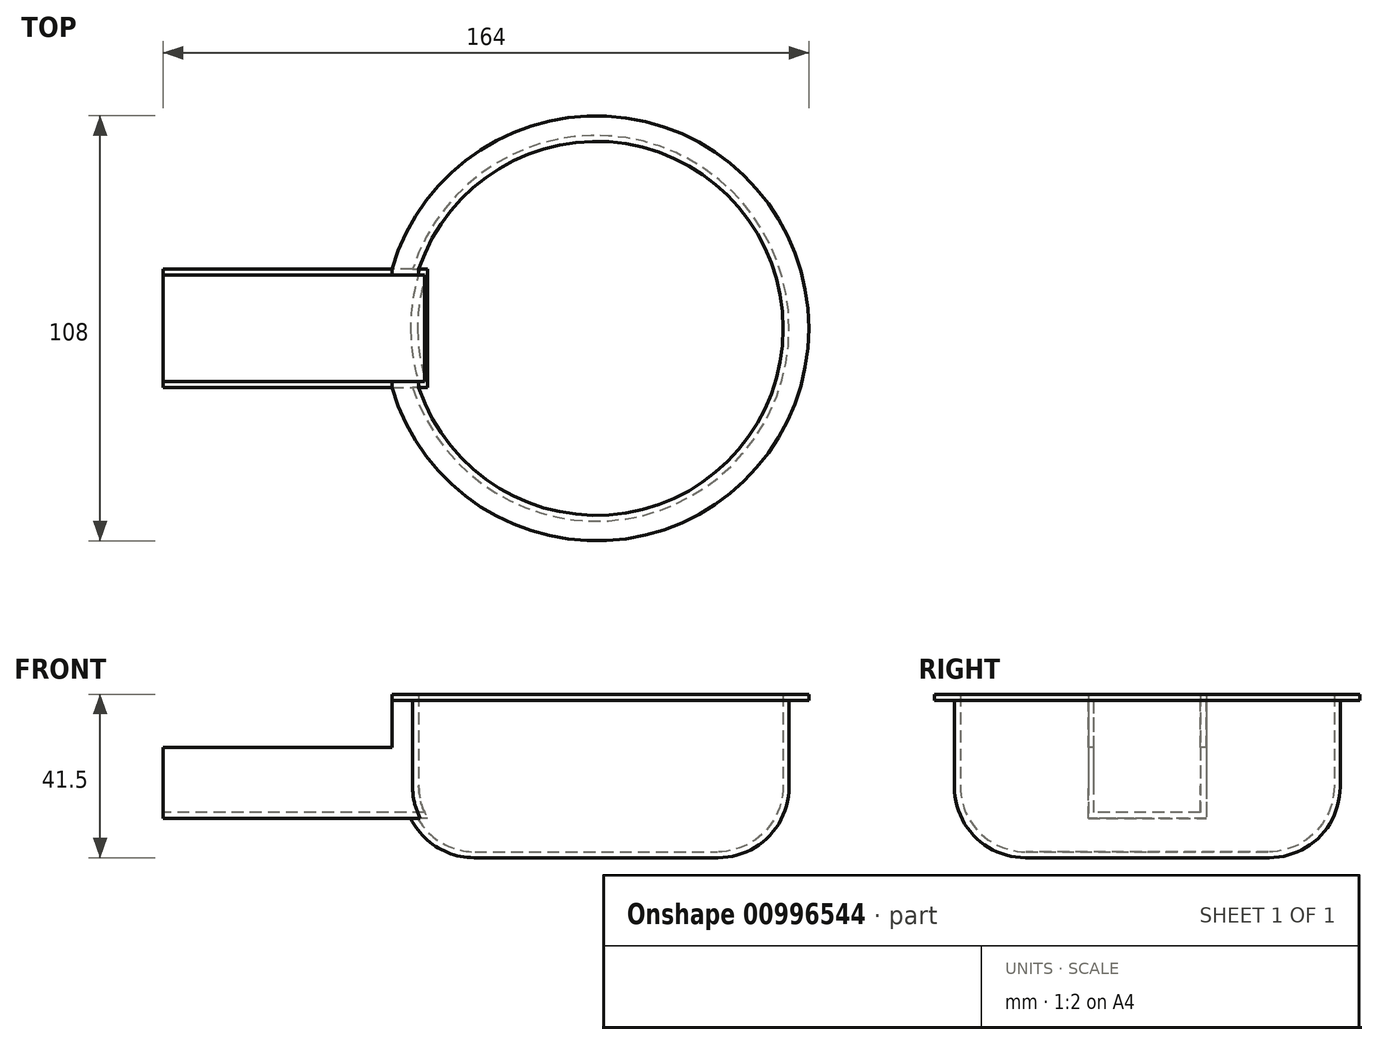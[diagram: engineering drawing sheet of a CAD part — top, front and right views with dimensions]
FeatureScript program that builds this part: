
annotation { "Feature Type Name" : "Feature", "Feature Type Description" : "" }
export const myFeature = defineFeature(function(context is Context, id is Id, definition is map)
    precondition{}
    {
        {
            var Q0;
            Q0=qCreatedBy(makeId("Top.planeOp"),FACE);
            var sketch = newSketch(context, id + "F0", { "sketchPlane" : qUnion([Q0])});
            skLineSegment(sketch, "E0", {"start": v(0, 0) * mm, "end": v(0, 15) * mm});
            skLineSegment(sketch, "E1", {"start": v(0, 15) * mm, "end": v(-110, 15) * mm});
            skLineSegment(sketch, "E2", {"start": v(-110, 15) * mm, "end": v(-110, -15) * mm});
            skLineSegment(sketch, "E3", {"start": v(-110, -15) * mm, "end": v(0, -15) * mm});
            skLineSegment(sketch, "E4", {"start": v(0, -15) * mm, "end": v(0, 0) * mm});
            skSolve(sketch);
        }
        {
            var Q0;
            Q0=qCreatedBy(makeId("Front.planeOp"),FACE);
            var sketch = newSketch(context, id + "F1", { "sketchPlane" : qUnion([Q0])});
            skLineSegment(sketch, "E5", {"start": v(0, 0) * mm, "end": v(30.8, 0) * mm});
            skLineSegment(sketch, "E6", {"start": v(47.5, 16.7) * mm, "end": v(47.5, 40) * mm});
            skLineSegment(sketch, "E7", {"start": v(47.5, 40) * mm, "end": v(54, 40) * mm});
            skLineSegment(sketch, "E8", {"start": v(54, 40) * mm, "end": v(54, 38.5) * mm});
            skLineSegment(sketch, "E9", {"start": v(54, 38.5) * mm, "end": v(49, 38.5) * mm});
            skLineSegment(sketch, "E10", {"start": v(49, 38.5) * mm, "end": v(49, 16.5) * mm});
            skLineSegment(sketch, "E11", {"start": v(31, -1.5) * mm, "end": v(0, -1.5) * mm});
            skLineSegment(sketch, "E12", {"start": v(0, -1.5) * mm, "end": v(0, 0) * mm});
            skPoint(sketch, "E13.visualSharp", {"position": v(47.5, 0) * mm});
            skArc(sketch, "E13.filletArc", {"start": v(30.8, 0) * mm, "mid": v(42.6, 4.9) * mm, "end": v(47.5, 16.7) * mm});
            skPoint(sketch, "E14.visualSharp", {"position": v(49, -1.5) * mm});
            skArc(sketch, "E14.filletArc", {"start": v(31, -1.5) * mm, "mid": v(43.73, 3.77) * mm, "end": v(49, 16.5) * mm});
            skLineSegment(sketch, "E15", {"start": v(0, 0) * mm, "end": v(0, 40) * mm});
            skLineSegment(sketch, "E16", {"start": v(0, 40) * mm, "end": v(47.5, 40) * mm});
            skSolve(sketch);
        }
        {
            var Q0;
            Q0=makeQuery(id+"F0.imprint","IMPRINT",FACE,{"disambiguationData":[TD([[makeQuery(id+"F0.imprint","IMPRINT",EDGE,{"derivedFrom":sQuery(id+"F0.wireOp",EDGE,"E0")}),1.0]])]});
            extrude(context, id + "F2", {"entities" : qUnion([Q0]), "depth" : 40 * mm, "offsetDistance" : 25 * mm});
        }
        {
            var Q0;
            Q0=makeQuery(id+"F0.imprint","IMPRINT",FACE,{"disambiguationData":[TD([[makeQuery(id+"F0.imprint","IMPRINT",EDGE,{"derivedFrom":sQuery(id+"F0.wireOp",EDGE,"E0")}),1.0]])]});
            extrude(context, id + "F3", {"entities" : qUnion([Q0]), "operationType" : NewBodyOperationType.REMOVE, "depth" : 8.5 * mm, "offsetDistance" : 25 * mm});
        }
        {
            var Q0;
            Q0=makeQuery(id+"F2.opExtrude","SWEPT_FACE",FACE,{"disambiguationData":[OSD([sQuery(id+"F0.wireOp",EDGE,"E2")])]});
            var sketch = newSketch(context, id + "F4", { "sketchPlane" : qUnion([Q0])});
            skLineSegment(sketch, "E17", {"start": v(-15, 40) * mm, "end": v(-13.5, 40) * mm});
            skLineSegment(sketch, "E18", {"start": v(-13.5, 40) * mm, "end": v(-13.5, 10) * mm});
            skLineSegment(sketch, "E19", {"start": v(-13.5, 10) * mm, "end": v(13.5, 10) * mm});
            skLineSegment(sketch, "E20", {"start": v(13.5, 10) * mm, "end": v(13.5, 40) * mm});
            skSolve(sketch);
        }
        {
            var Q0;
            Q0=makeQuery(id+"F1.imprint","IMPRINT",FACE,{"disambiguationData":[TD([[makeQuery(id+"F1.imprint","IMPRINT",EDGE,{"derivedFrom":sQuery(id+"F1.wireOp",EDGE,"E5")}),-1.0]])]});
            var Q1;
            Q1=sQuery(id+"F1.wireOp",EDGE,"E12");
            revolve(context, id + "F5", {"operationType" : NewBodyOperationType.ADD, "surfaceOperationType" : NewSurfaceOperationType.NEW, "entities" : qUnion([Q0]), "axis" : qUnion([Q1]), "revolveType" : RevolveType.FULL});
        }
        {
            var Q0;
            {var subQ0=sQuery(id+"F4.wireOp",EDGE,"E18");Q0=makeQuery(id+"F4.imprint","IMPRINT",FACE,{"disambiguationData":[TD([[makeQuery(id+"F4.imprint","IMPRINT",EDGE,{"derivedFrom":subQ0}),1.0]])]});}
            extrude(context, id + "F6", {"entities" : qUnion([Q0]), "operationType" : NewBodyOperationType.REMOVE, "oppositeDirection" : true, "depth" : 110 * mm, "offsetDistance" : 25 * mm});
        }
        {
            var Q0;
            {var subQ1=sQuery(id+"F0.wireOp",EDGE,"E3");Q0=makeQuery(id+"F5.boolean.opBoolean","SPLIT",FACE,{"disambiguationData":[TD([makeQuery(id+"F5.opRevolve","SWEPT_FACE",FACE,{"disambiguationData":[OSD([sQuery(id+"F1.wireOp",EDGE,"E6")])]})])],"derivedFrom":makeQuery(id+"F2.opExtrude","SWEPT_FACE",FACE,{"disambiguationData":[OSD([subQ1])]})});}
            extrude(context, id + "F7", {"entities" : qUnion([Q0]), "operationType" : NewBodyOperationType.REMOVE, "oppositeDirection" : true, "depth" : 30 * mm, "offsetDistance" : 25 * mm});
        }
        {
            var Q0;
            Q0=makeQuery(id+"F5.boolean.opBoolean","MERGE",FACE,{"derivedFrom":[makeQuery(id+"F2.opExtrude","CAP_FACE",FACE,{"disambiguationData":[OSD([sQuery(id+"F0.wireOp",EDGE,"E0"),sQuery(id+"F0.wireOp",EDGE,"E1"),sQuery(id+"F0.wireOp",EDGE,"E2"),sQuery(id+"F0.wireOp",EDGE,"E3"),sQuery(id+"F0.wireOp",EDGE,"E4")])],"isStart":false}),makeQuery(id+"F5.opRevolve","SWEPT_FACE",FACE,{"disambiguationData":[OSD([sQuery(id+"F1.wireOp",EDGE,"E7")])]})]});
            var sketch = newSketch(context, id + "F8", { "sketchPlane" : qUnion([Q0])});
            skLineSegment(sketch, "E21", {"start": v(-51.87, -15) * mm, "end": v(-51.87, -13.5) * mm});
            skLineSegment(sketch, "E22", {"start": v(-51.87, 15) * mm, "end": v(-51.87, 13.5) * mm});
            skSolve(sketch);
        }
        {
            var Q0;
            {var subQ0=sQuery(id+"F8.wireOp",EDGE,"E21");Q0=makeQuery(id+"F8.imprint","IMPRINT",FACE,{"disambiguationData":[TD([[makeQuery(id+"F8.imprint","IMPRINT",EDGE,{"derivedFrom":subQ0}),1.0]])]});}
            var Q1;
            {var subQ0=sQuery(id+"F8.wireOp",EDGE,"E22");Q1=makeQuery(id+"F8.imprint","IMPRINT",FACE,{"disambiguationData":[TD([[makeQuery(id+"F8.imprint","IMPRINT",EDGE,{"derivedFrom":subQ0}),-1.0]])]});}
            extrude(context, id + "F9", {"entities" : qUnion([Q0, Q1]), "operationType" : NewBodyOperationType.REMOVE, "oppositeDirection" : true, "depth" : 13.5 * mm, "offsetDistance" : 25 * mm});
        }
    });
